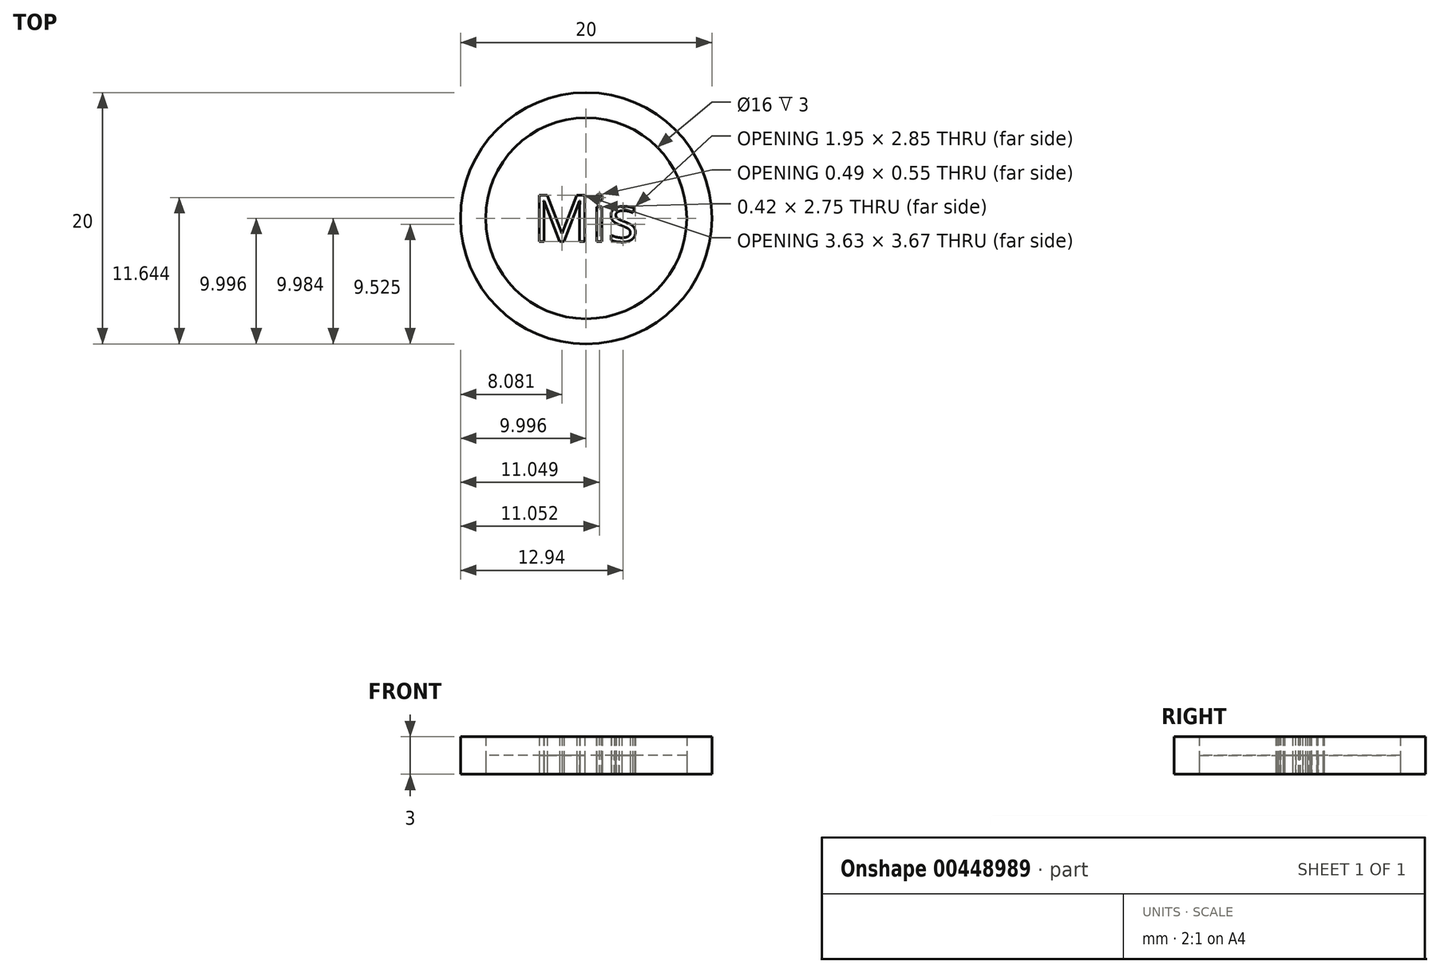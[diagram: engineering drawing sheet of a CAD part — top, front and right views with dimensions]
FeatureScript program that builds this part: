
annotation { "Feature Type Name" : "Feature", "Feature Type Description" : "" }
export const myFeature = defineFeature(function(context is Context, id is Id, definition is map)
    precondition{}
    {
        {
            var Q0;
            Q0=qCreatedBy(makeId("Top.planeOp"),FACE);
            var sketch = newSketch(context, id + "F0", { "sketchPlane" : qUnion([Q0])});
            skText(sketch, "E0", { "text": "Mis", "fontName": "OpenSans-Regular.ttf"});
            skCircle(sketch, "E1", {"center": v(-7.13, 1.85) * mm, "radius": 10 * mm});
            skCircle(sketch, "E2", {"center": v(-7.13, 1.85) * mm, "radius": 8 * mm});
            const initialGuessF0  = {"E0": [-0.01137, 0, 1, 0, 0.0037]};
            skSetInitialGuess(sketch, initialGuessF0);
            skSolve(sketch);
        }
        {
            var Q0;
            Q0=makeQuery(id+"F0.imprint","IMPRINT",FACE,{"disambiguationData":[TD([[makeQuery(id+"F0.imprint","IMPRINT",EDGE,{"derivedFrom":sQuery(id+"F0.wireOp",EDGE,"E1")}),1.0]])]});
            var Q1;
            Q1=makeQuery(id+"F0.imprint","IMPRINT",FACE,{"disambiguationData":[TD([[makeQuery(id+"F0.imprint","IMPRINT",EDGE,{"derivedFrom":sQuery(id+"F0.wireOp",EDGE,"E0.sketch_text.stroke-18")}),-1.0]])]});
            var Q2;
            Q2=makeQuery(id+"F0.imprint","IMPRINT",FACE,{"disambiguationData":[TD([[makeQuery(id+"F0.imprint","IMPRINT",EDGE,{"derivedFrom":sQuery(id+"F0.wireOp",EDGE,"E0.sketch_text.stroke-22")}),-1.0]])]});
            var Q3;
            Q3=makeQuery(id+"F0.imprint","IMPRINT",FACE,{"disambiguationData":[TD([[makeQuery(id+"F0.imprint","IMPRINT",EDGE,{"derivedFrom":sQuery(id+"F0.wireOp",EDGE,"E0.sketch_text.stroke-30")}),-1.0]])]});
            var Q4;
            Q4=makeQuery(id+"F0.imprint","IMPRINT",FACE,{"disambiguationData":[TD([[makeQuery(id+"F0.imprint","IMPRINT",EDGE,{"derivedFrom":sQuery(id+"F0.wireOp",EDGE,"E0.sketch_text.stroke-0")}),-1.0]])]});
            extrude(context, id + "F1", {"entities" : qUnion([Q0, Q1, Q2, Q3, Q4]), "depth" : 3 * mm});
        }
        {
            var Q0;
            Q0=makeQuery(id+"F0.imprint","IMPRINT",FACE,{"disambiguationData":[TD([[makeQuery(id+"F0.imprint","IMPRINT",EDGE,{"derivedFrom":sQuery(id+"F0.wireOp",EDGE,"E0.sketch_text.stroke-0")}),1.0]])]});
            extrude(context, id + "F2", {"entities" : qUnion([Q0]), "depth" : 1.5 * mm});
        }
    });
